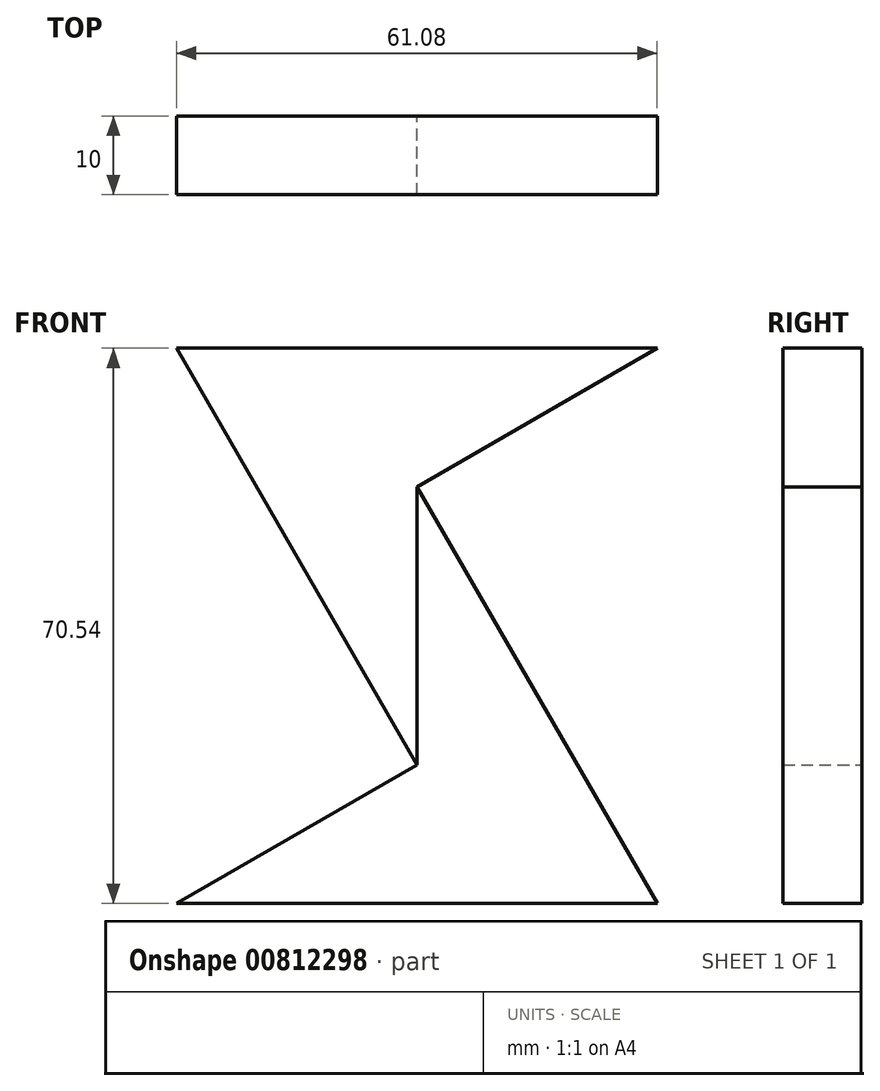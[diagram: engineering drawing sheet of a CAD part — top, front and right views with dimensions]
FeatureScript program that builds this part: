
annotation { "Feature Type Name" : "Feature", "Feature Type Description" : "" }
export const myFeature = defineFeature(function(context is Context, id is Id, definition is map)
    precondition{}
    {
        {
            var Q0;
            Q0=qCreatedBy(makeId("Front.planeOp"),FACE);
            var sketch = newSketch(context, id + "F0", { "sketchPlane" : qUnion([Q0])});
            skCircle(sketch, "E0.cCircle", {"center": v(0, 17.63) * mm, "radius": 17.63 * mm, "construction": true});
            skLineSegment(sketch, "E0.0", {"start": v(-30.54, 35.27) * mm, "end": v(30.54, 35.27) * mm});
            skLineSegment(sketch, "E0.1", {"start": v(30.54, 35.27) * mm, "end": v(0, -17.63) * mm});
            skLineSegment(sketch, "E0.2", {"start": v(0, -17.63) * mm, "end": v(-30.54, 35.27) * mm});
            skPoint(sketch, "E0.0.midPoint", {"position": v(0, 35.27) * mm});
            skCircle(sketch, "E1.cCircle", {"center": v(0, -17.63) * mm, "radius": 17.63 * mm, "construction": true});
            skLineSegment(sketch, "E1.0", {"start": v(30.54, -35.27) * mm, "end": v(-30.54, -35.27) * mm});
            skLineSegment(sketch, "E1.1", {"start": v(-30.54, -35.27) * mm, "end": v(0, 17.63) * mm});
            skLineSegment(sketch, "E1.2", {"start": v(0, 17.63) * mm, "end": v(30.54, -35.27) * mm});
            skPoint(sketch, "E1.0.midPoint", {"position": v(0, -35.27) * mm});
            skLineSegment(sketch, "E2", {"start": v(0, 17.63) * mm, "end": v(0, -17.63) * mm});
            skLineSegment(sketch, "E3", {"start": v(0, 17.63) * mm, "end": v(30.54, 35.27) * mm});
            skLineSegment(sketch, "E4", {"start": v(0, -17.63) * mm, "end": v(-30.54, -35.27) * mm});
            skSolve(sketch);
        }
        {
            var Q0;
            {var subQ0=sQuery(id+"F0.wireOp",EDGE,"E2");Q0=makeQuery(id+"F0.imprint","IMPRINT",FACE,{"disambiguationData":[TD([[makeQuery(id+"F0.imprint","IMPRINT",EDGE,{"derivedFrom":subQ0}),-1.0]])]});}
            var Q1;
            {var subQ0=sQuery(id+"F0.wireOp",EDGE,"E0.0");Q1=makeQuery(id+"F0.imprint","IMPRINT",FACE,{"disambiguationData":[TD([[makeQuery(id+"F0.imprint","IMPRINT",EDGE,{"derivedFrom":subQ0}),-1.0]])]});}
            extrude(context, id + "F1", {"entities" : qUnion([Q0, Q1]), "endBound" : BoundingType.SYMMETRIC, "depth" : 10 * mm, "offsetDistance" : 25 * mm});
        }
        {
            var Q0;
            {var subQ0=sQuery(id+"F0.wireOp",EDGE,"E2");Q0=makeQuery(id+"F0.imprint","IMPRINT",FACE,{"disambiguationData":[TD([[makeQuery(id+"F0.imprint","IMPRINT",EDGE,{"derivedFrom":subQ0}),1.0]])]});}
            var Q1;
            {var subQ4=sQuery(id+"F0.wireOp",EDGE,"E1.0");Q1=makeQuery(id+"F0.imprint","IMPRINT",FACE,{"disambiguationData":[TD([[makeQuery(id+"F0.imprint","IMPRINT",EDGE,{"derivedFrom":subQ4}),-1.0]])]});}
            extrude(context, id + "F2", {"entities" : qUnion([Q0, Q1]), "endBound" : BoundingType.SYMMETRIC, "depth" : 10 * mm, "offsetDistance" : 25 * mm});
        }
    });
